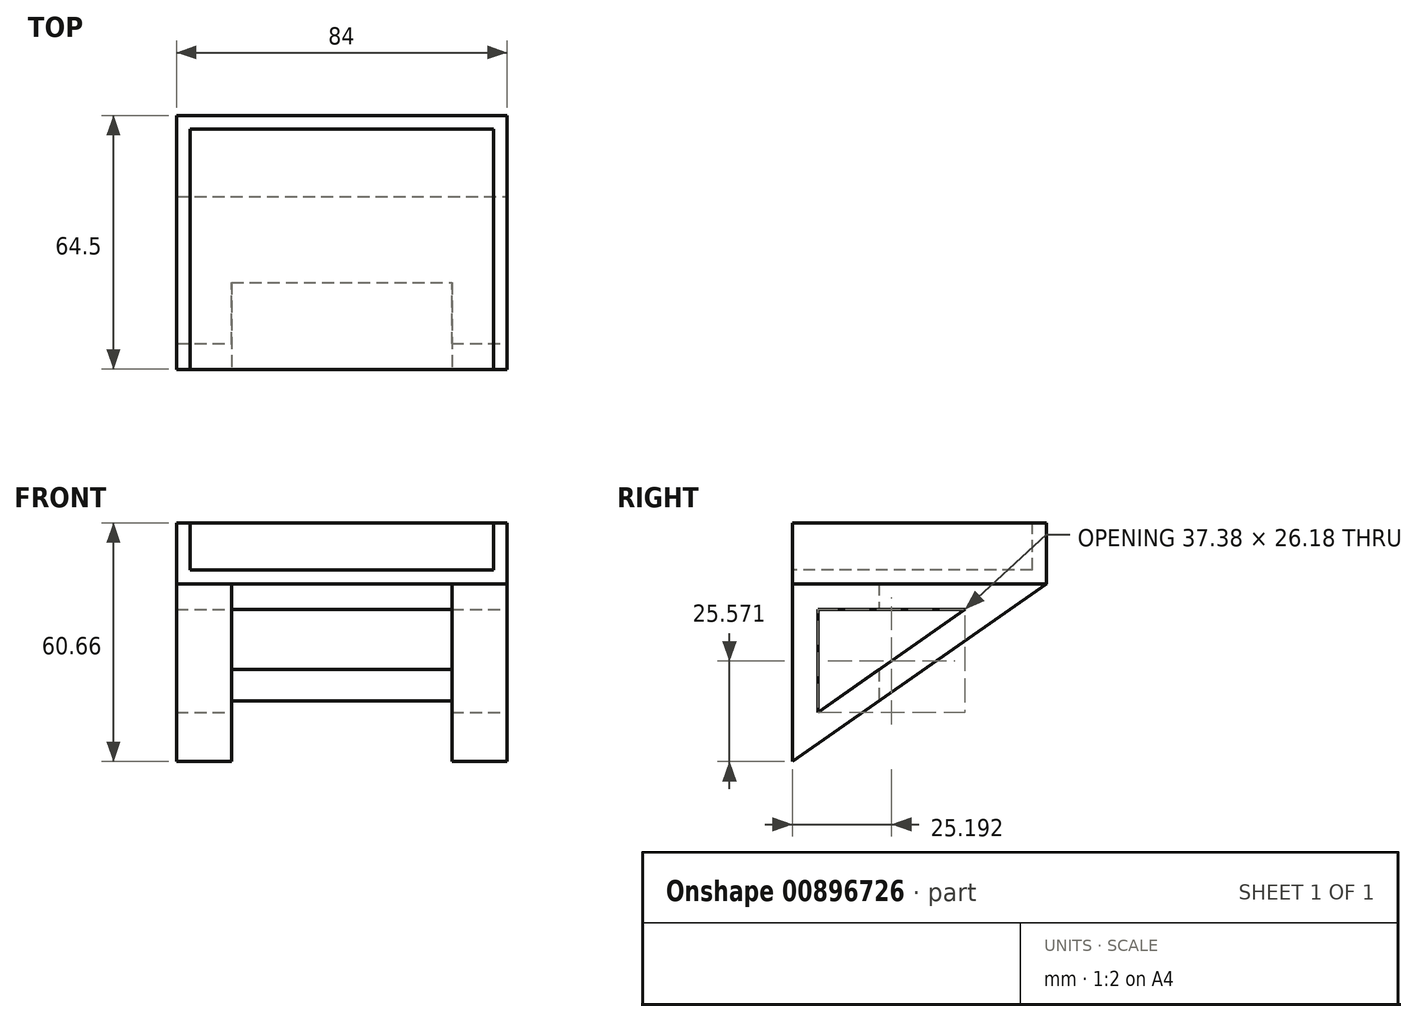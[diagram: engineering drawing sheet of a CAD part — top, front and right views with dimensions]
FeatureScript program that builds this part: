
annotation { "Feature Type Name" : "Feature", "Feature Type Description" : "" }
export const myFeature = defineFeature(function(context is Context, id is Id, definition is map)
    precondition{}
    {
        {
            var Q0;
            Q0=qCreatedBy(makeId("Top.planeOp"),FACE);
            var sketch = newSketch(context, id + "F0", { "sketchPlane" : qUnion([Q0])});
            skLineSegment(sketch, "E0", {"start": v(-183.18, 173.7) * mm, "end": v(-106.18, 173.7) * mm});
            skLineSegment(sketch, "E1", {"start": v(-183.18, 173.7) * mm, "end": v(-183.18, 112.7) * mm});
            skLineSegment(sketch, "E2", {"start": v(-183.18, 112.7) * mm, "end": v(-106.18, 112.7) * mm});
            skLineSegment(sketch, "E3", {"start": v(-106.18, 112.7) * mm, "end": v(-106.18, 173.7) * mm});
            skSolve(sketch);
        }
        {
            var Q0;
            Q0=makeQuery(id+"F0.imprint","IMPRINT",FACE,{"disambiguationData":[TD([[makeQuery(id+"F0.imprint","IMPRINT",EDGE,{"derivedFrom":sQuery(id+"F0.wireOp",EDGE,"E0")}),-1.0]])]});
            extrude(context, id + "F1", {"entities" : qUnion([Q0]), "depth" : 3.5 * mm, "offsetDistance" : 25 * mm});
        }
        {
            var Q0;
            Q0=makeQuery(id+"F1.opExtrude","CAP_FACE",FACE,{"disambiguationData":[OSD([sQuery(id+"F0.wireOp",EDGE,"E0"),sQuery(id+"F0.wireOp",EDGE,"E1"),sQuery(id+"F0.wireOp",EDGE,"E2"),sQuery(id+"F0.wireOp",EDGE,"E3")])],"isStart":false});
            var sketch = newSketch(context, id + "F2", { "sketchPlane" : qUnion([Q0])});
            skLineSegment(sketch, "E4", {"start": v(-183.18, 173.7) * mm, "end": v(-186.68, 173.7) * mm});
            skLineSegment(sketch, "E5", {"start": v(-186.68, 173.7) * mm, "end": v(-186.68, 112.7) * mm});
            skLineSegment(sketch, "E6", {"start": v(-186.68, 112.7) * mm, "end": v(-183.18, 112.7) * mm});
            skLineSegment(sketch, "E7", {"start": v(-106.18, 173.7) * mm, "end": v(-102.68, 173.7) * mm});
            skLineSegment(sketch, "E8", {"start": v(-102.68, 173.7) * mm, "end": v(-102.68, 112.7) * mm});
            skLineSegment(sketch, "E9", {"start": v(-102.68, 112.7) * mm, "end": v(-106.18, 112.7) * mm});
            skLineSegment(sketch, "E10", {"start": v(-102.68, 112.7) * mm, "end": v(-102.68, 109.2) * mm});
            skLineSegment(sketch, "E11", {"start": v(-186.68, 112.7) * mm, "end": v(-186.68, 101.46) * mm, "construction": true});
            skLineSegment(sketch, "E12", {"start": v(-102.68, 109.2) * mm, "end": v(-186.68, 109.2) * mm});
            skLineSegment(sketch, "E13", {"start": v(-186.68, 109.2) * mm, "end": v(-186.68, 112.7) * mm});
            skSolve(sketch);
        }
        {
            var Q0;
            Q0=makeQuery(id+"F2.imprint","IMPRINT",FACE,{"disambiguationData":[TD([[makeQuery(id+"F2.imprint","IMPRINT",EDGE,{"derivedFrom":sQuery(id+"F2.wireOp",EDGE,"E4")}),1.0]])]});
            var Q1;
            Q1=makeQuery(id+"F2.imprint","IMPRINT",FACE,{"disambiguationData":[TD([[makeQuery(id+"F2.imprint","IMPRINT",EDGE,{"derivedFrom":sQuery(id+"F2.wireOp",EDGE,"E6")}),-1.0]])]});
            var Q2;
            Q2=makeQuery(id+"F2.imprint","IMPRINT",FACE,{"disambiguationData":[TD([[makeQuery(id+"F2.imprint","IMPRINT",EDGE,{"derivedFrom":sQuery(id+"F2.wireOp",EDGE,"E7")}),-1.0]])]});
            extrude(context, id + "F3", {"entities" : qUnion([Q0, Q1, Q2]), "depth" : 12 * mm, "offsetDistance" : 25 * mm});
        }
        {
            var Q0;
            Q0=makeQuery(id+"F3.opExtrude","CAP_FACE",FACE,{"disambiguationData":[OSD([sQuery(id+"F0.wireOp",EDGE,"E1"),sQuery(id+"F0.wireOp",EDGE,"E2"),sQuery(id+"F0.wireOp",EDGE,"E3"),sQuery(id+"F2.wireOp",EDGE,"E4"),sQuery(id+"F2.wireOp",EDGE,"E5"),sQuery(id+"F2.wireOp",EDGE,"E7"),sQuery(id+"F2.wireOp",EDGE,"E8"),sQuery(id+"F2.wireOp",EDGE,"E10"),sQuery(id+"F2.wireOp",EDGE,"E12"),sQuery(id+"F2.wireOp",EDGE,"E13")])],"isStart":true});
            extrude(context, id + "F4", {"entities" : qUnion([Q0]), "depth" : 3.5 * mm, "offsetDistance" : 25 * mm});
        }
        {
            var Q0;
            Q0=makeQuery(id+"F4.opExtrude","SWEPT_FACE",FACE,{"disambiguationData":[OSD([sQuery(id+"F2.wireOp",EDGE,"E8"),sQuery(id+"F2.wireOp",EDGE,"E10")])]});
            var sketch = newSketch(context, id + "F5", { "sketchPlane" : qUnion([Q0])});
            skLineSegment(sketch, "E14", {"start": v(109.2, 0) * mm, "end": v(109.2, -21.78) * mm, "construction": true});
            skLineSegment(sketch, "E15", {"start": v(173.7, 0) * mm, "end": v(139.43, -24) * mm});
            skLineSegment(sketch, "E16", {"start": v(109.2, -24) * mm, "end": v(109.2, 0) * mm});
            skLineSegment(sketch, "E17", {"start": v(139.43, -24) * mm, "end": v(109.2, -24) * mm});
            skLineSegment(sketch, "E18", {"start": v(139.43, -24) * mm, "end": v(109.2, -45.16) * mm});
            skLineSegment(sketch, "E19", {"start": v(109.2, -45.16) * mm, "end": v(109.2, -24) * mm});
            skLineSegment(sketch, "E20", {"start": v(115.7, -32.68) * mm, "end": v(153.1, -6.5) * mm});
            skLineSegment(sketch, "E21", {"start": v(153.1, -6.5) * mm, "end": v(115.7, -6.5) * mm});
            skLineSegment(sketch, "E22", {"start": v(115.7, -6.5) * mm, "end": v(115.7, -32.68) * mm});
            skSolve(sketch);
        }
        {
            var Q0;
            {var subQ4=sQuery(id+"F5.wireOp",EDGE,"E15");Q0=makeQuery(id+"F5.imprint","IMPRINT",FACE,{"disambiguationData":[TD([[makeQuery(id+"F5.imprint","IMPRINT",EDGE,{"derivedFrom":subQ4}),-1.0]])]});}
            var Q1;
            {var subQ1=sQuery(id+"F5.wireOp",EDGE,"E18");Q1=makeQuery(id+"F5.imprint","IMPRINT",FACE,{"disambiguationData":[TD([[makeQuery(id+"F5.imprint","IMPRINT",EDGE,{"derivedFrom":subQ1}),-1.0]])]});}
            extrude(context, id + "F6", {"entities" : qUnion([Q0, Q1]), "oppositeDirection" : true, "depth" : 84 * mm, "offsetDistance" : 25 * mm});
        }
        {
            var Q0;
            Q0=makeQuery(id+"F6.opExtrude","SWEPT_FACE",FACE,{"disambiguationData":[OSD([sQuery(id+"F5.wireOp",EDGE,"E16"),sQuery(id+"F5.wireOp",EDGE,"E19")])]});
            var sketch = newSketch(context, id + "F7", { "sketchPlane" : qUnion([Q0])});
            skLineSegment(sketch, "E23", {"start": v(-172.68, 0) * mm, "end": v(-172.68, -45.16) * mm});
            skLineSegment(sketch, "E24", {"start": v(-116.68, 0) * mm, "end": v(-116.68, -45.16) * mm});
            skSolve(sketch);
        }
        {
            var Q0;
            {var subQ0=sQuery(id+"F7.wireOp",EDGE,"E23");Q0=makeQuery(id+"F7.imprint","IMPRINT",FACE,{"disambiguationData":[TD([[makeQuery(id+"F7.imprint","IMPRINT",EDGE,{"derivedFrom":subQ0}),1.0]])]});}
            extrude(context, id + "F8", {"entities" : qUnion([Q0]), "operationType" : NewBodyOperationType.REMOVE, "oppositeDirection" : true, "depth" : 22 * mm, "offsetDistance" : 25 * mm});
        }
        {
            var Q0;
            Q0=makeQuery(id+"F3.opExtrude","SWEPT_FACE",FACE,{"disambiguationData":[OSD([sQuery(id+"F2.wireOp",EDGE,"E12")])]});
            var sketch = newSketch(context, id + "F9", { "sketchPlane" : qUnion([Q0])});
            skLineSegment(sketch, "E25", {"start": v(-183.18, 3.5) * mm, "end": v(-183.18, 15.5) * mm});
            skLineSegment(sketch, "E26", {"start": v(-106.18, 3.5) * mm, "end": v(-106.18, 15.5) * mm});
            skSolve(sketch);
        }
        {
            var Q0;
            {var subQ0=sQuery(id+"F9.wireOp",EDGE,"E25");Q0=makeQuery(id+"F9.imprint","IMPRINT",FACE,{"disambiguationData":[TD([[makeQuery(id+"F9.imprint","IMPRINT",EDGE,{"derivedFrom":subQ0}),-1.0]])]});}
            extrude(context, id + "F10", {"entities" : qUnion([Q0]), "operationType" : NewBodyOperationType.REMOVE, "oppositeDirection" : true, "depth" : 25 * mm, "offsetDistance" : 25 * mm});
        }
        {
            var Q0;
            Q0=makeQuery(id+"F1.opExtrude","SWEPT_FACE",FACE,{"disambiguationData":[OSD([sQuery(id+"F0.wireOp",EDGE,"E0")])]});
            var sketch = newSketch(context, id + "F11", { "sketchPlane" : qUnion([Q0])});
            skLineSegment(sketch, "E27", {"start": v(106.18, 15.5) * mm, "end": v(183.22, 15.5) * mm});
            skLineSegment(sketch, "E28", {"start": v(183.22, 15.5) * mm, "end": v(183.18, 3.5) * mm});
            skLineSegment(sketch, "E29", {"start": v(183.18, 3.5) * mm, "end": v(106.18, 3.5) * mm});
            skLineSegment(sketch, "E30", {"start": v(106.18, 3.5) * mm, "end": v(106.18, 15.5) * mm});
            skSolve(sketch);
        }
        {
            var Q0;
            Q0=makeQuery(id+"F11.imprint","IMPRINT",FACE,{"disambiguationData":[TD([[makeQuery(id+"F11.imprint","IMPRINT",EDGE,{"derivedFrom":sQuery(id+"F11.wireOp",EDGE,"E27")}),-1.0]])]});
            extrude(context, id + "F12", {"entities" : qUnion([Q0]), "operationType" : NewBodyOperationType.ADD, "oppositeDirection" : true, "depth" : 3.5 * mm, "offsetDistance" : 25 * mm});
        }
    });
